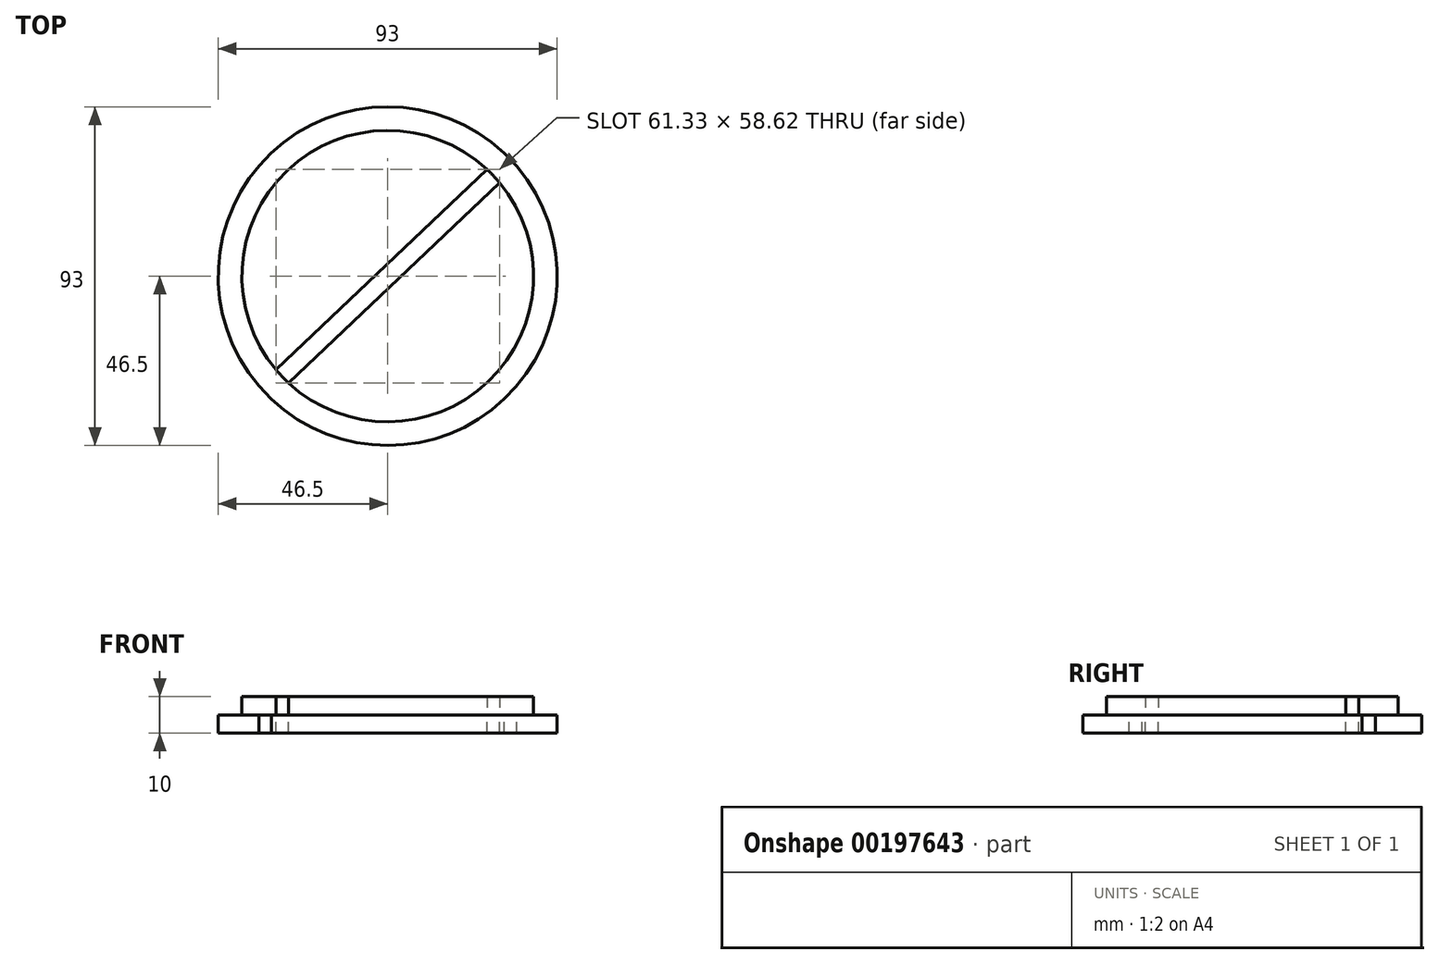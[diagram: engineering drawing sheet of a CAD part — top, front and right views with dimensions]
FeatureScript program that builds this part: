
annotation { "Feature Type Name" : "Feature", "Feature Type Description" : "" }
export const myFeature = defineFeature(function(context is Context, id is Id, definition is map)
    precondition{}
    {
        {
            var Q0;
            Q0=qCreatedBy(makeId("Top.planeOp"),FACE);
            var sketch = newSketch(context, id + "F0", { "sketchPlane" : qUnion([Q0])});
            skCircle(sketch, "E0", {"center": v(0, 0) * mm, "radius": 40 * mm});
            skCircle(sketch, "E1", {"center": v(0, 0) * mm, "radius": 46.5 * mm});
            skLineSegment(sketch, "E2", {"start": v(0, 0) * mm, "end": v(1.72, -1.81) * mm});
            skLineSegment(sketch, "E3", {"start": v(1.72, -1.81) * mm, "end": v(0, 0) * mm});
            skLineSegment(sketch, "E4", {"start": v(0, 0) * mm, "end": v(-1.72, 1.81) * mm});
            skLineSegment(sketch, "E5", {"start": v(-1.72, 1.81) * mm, "end": v(-35.38, -30.17) * mm});
            skLineSegment(sketch, "E6", {"start": v(-35.38, -30.17) * mm, "end": v(-31.94, -33.8) * mm});
            skLineSegment(sketch, "E7", {"start": v(-31.94, -33.8) * mm, "end": v(1.72, -1.81) * mm});
            skLineSegment(sketch, "E8", {"start": v(1.72, -1.81) * mm, "end": v(35.38, 30.17) * mm});
            skLineSegment(sketch, "E9", {"start": v(35.38, 30.17) * mm, "end": v(31.94, 33.8) * mm});
            skLineSegment(sketch, "E10", {"start": v(31.94, 33.8) * mm, "end": v(-1.72, 1.81) * mm});
            skSolve(sketch);
        }
        {
            var Q0;
            {var subQ6=sQuery(id+"F0.wireOp",EDGE,"E3");Q0=makeQuery(id+"F0.imprint","IMPRINT",FACE,{"disambiguationData":[TD([[makeQuery(id+"F0.imprint","IMPRINT",EDGE,{"derivedFrom":subQ6}),1.0]])]});}
            var Q1;
            {var subQ1=sQuery(id+"F0.wireOp",EDGE,"E3");Q1=makeQuery(id+"F0.imprint","IMPRINT",FACE,{"disambiguationData":[TD([[makeQuery(id+"F0.imprint","IMPRINT",EDGE,{"derivedFrom":subQ1}),-1.0]])]});}
            var Q2;
            {var subQ0=sQuery(id+"F0.wireOp",EDGE,"E10");var subQ1=sQuery(id+"F0.wireOp",EDGE,"E0");var subQ2=makeQuery(id+"F0.imprint","INTERSECT",VERTEX,{"derivedFrom":[subQ1,subQ0]});Q2=makeQuery(id+"F0.imprint","IMPRINT",FACE,{"disambiguationData":[TD([[makeQuery(id+"F0.imprint","IMPRINT",EDGE,{"disambiguationData":[TD([[subQ2,-1.0]])],"derivedFrom":subQ1}),1.0]])]});}
            var Q3;
            {var subQ0=sQuery(id+"F0.wireOp",EDGE,"E8");var subQ1=sQuery(id+"F0.wireOp",EDGE,"E0");var subQ2=makeQuery(id+"F0.imprint","INTERSECT",VERTEX,{"derivedFrom":[subQ1,subQ0]});Q3=makeQuery(id+"F0.imprint","IMPRINT",FACE,{"disambiguationData":[TD([[makeQuery(id+"F0.imprint","IMPRINT",EDGE,{"disambiguationData":[TD([[subQ2,1.0]])],"derivedFrom":subQ1}),1.0]])]});}
            extrude(context, id + "F1", {"entities" : qUnion([Q0, Q1, Q2, Q3]), "depth" : 5 * mm});
        }
        {
            var Q0;
            {var subQ1=sQuery(id+"F0.wireOp",EDGE,"E3");Q0=makeQuery(id+"F0.imprint","IMPRINT",FACE,{"disambiguationData":[TD([[makeQuery(id+"F0.imprint","IMPRINT",EDGE,{"derivedFrom":subQ1}),-1.0]])]});}
            var Q1;
            {var subQ6=sQuery(id+"F0.wireOp",EDGE,"E3");Q1=makeQuery(id+"F0.imprint","IMPRINT",FACE,{"disambiguationData":[TD([[makeQuery(id+"F0.imprint","IMPRINT",EDGE,{"derivedFrom":subQ6}),1.0]])]});}
            var Q2;
            {var subQ5=sQuery(id+"F0.wireOp",EDGE,"E9");Q2=makeQuery(id+"F0.imprint","IMPRINT",FACE,{"disambiguationData":[TD([[makeQuery(id+"F0.imprint","IMPRINT",EDGE,{"derivedFrom":subQ5}),1.0]])]});}
            var Q3;
            {var subQ5=sQuery(id+"F0.wireOp",EDGE,"E6");Q3=makeQuery(id+"F0.imprint","IMPRINT",FACE,{"disambiguationData":[TD([[makeQuery(id+"F0.imprint","IMPRINT",EDGE,{"derivedFrom":subQ5}),1.0]])]});}
            var Q4;
            {var subQ0=sQuery(id+"F0.wireOp",EDGE,"E8");var subQ1=sQuery(id+"F0.wireOp",EDGE,"E0");var subQ2=makeQuery(id+"F0.imprint","INTERSECT",VERTEX,{"derivedFrom":[subQ1,subQ0]});Q4=makeQuery(id+"F0.imprint","IMPRINT",FACE,{"disambiguationData":[TD([[makeQuery(id+"F0.imprint","IMPRINT",EDGE,{"disambiguationData":[TD([[subQ2,1.0]])],"derivedFrom":subQ1}),-1.0]])]});}
            var Q5;
            {var subQ0=sQuery(id+"F0.wireOp",EDGE,"E10");var subQ1=sQuery(id+"F0.wireOp",EDGE,"E0");var subQ2=makeQuery(id+"F0.imprint","INTERSECT",VERTEX,{"derivedFrom":[subQ1,subQ0]});Q5=makeQuery(id+"F0.imprint","IMPRINT",FACE,{"disambiguationData":[TD([[makeQuery(id+"F0.imprint","IMPRINT",EDGE,{"disambiguationData":[TD([[subQ2,-1.0]])],"derivedFrom":subQ1}),-1.0]])]});}
            var Q6;
            {var subQ0=sQuery(id+"F0.wireOp",EDGE,"E8");var subQ1=sQuery(id+"F0.wireOp",EDGE,"E0");var subQ2=makeQuery(id+"F0.imprint","INTERSECT",VERTEX,{"derivedFrom":[subQ1,subQ0]});Q6=makeQuery(id+"F0.imprint","IMPRINT",FACE,{"disambiguationData":[TD([[makeQuery(id+"F0.imprint","IMPRINT",EDGE,{"disambiguationData":[TD([[subQ2,1.0]])],"derivedFrom":subQ1}),1.0]])]});}
            var Q7;
            {var subQ0=sQuery(id+"F0.wireOp",EDGE,"E10");var subQ1=sQuery(id+"F0.wireOp",EDGE,"E0");var subQ2=makeQuery(id+"F0.imprint","INTERSECT",VERTEX,{"derivedFrom":[subQ1,subQ0]});Q7=makeQuery(id+"F0.imprint","IMPRINT",FACE,{"disambiguationData":[TD([[makeQuery(id+"F0.imprint","IMPRINT",EDGE,{"disambiguationData":[TD([[subQ2,-1.0]])],"derivedFrom":subQ1}),1.0]])]});}
            extrude(context, id + "F2", {"entities" : qUnion([Q0, Q1, Q2, Q3, Q4, Q5, Q6, Q7]), "oppositeDirection" : true, "depth" : 5 * mm});
        }
    });
